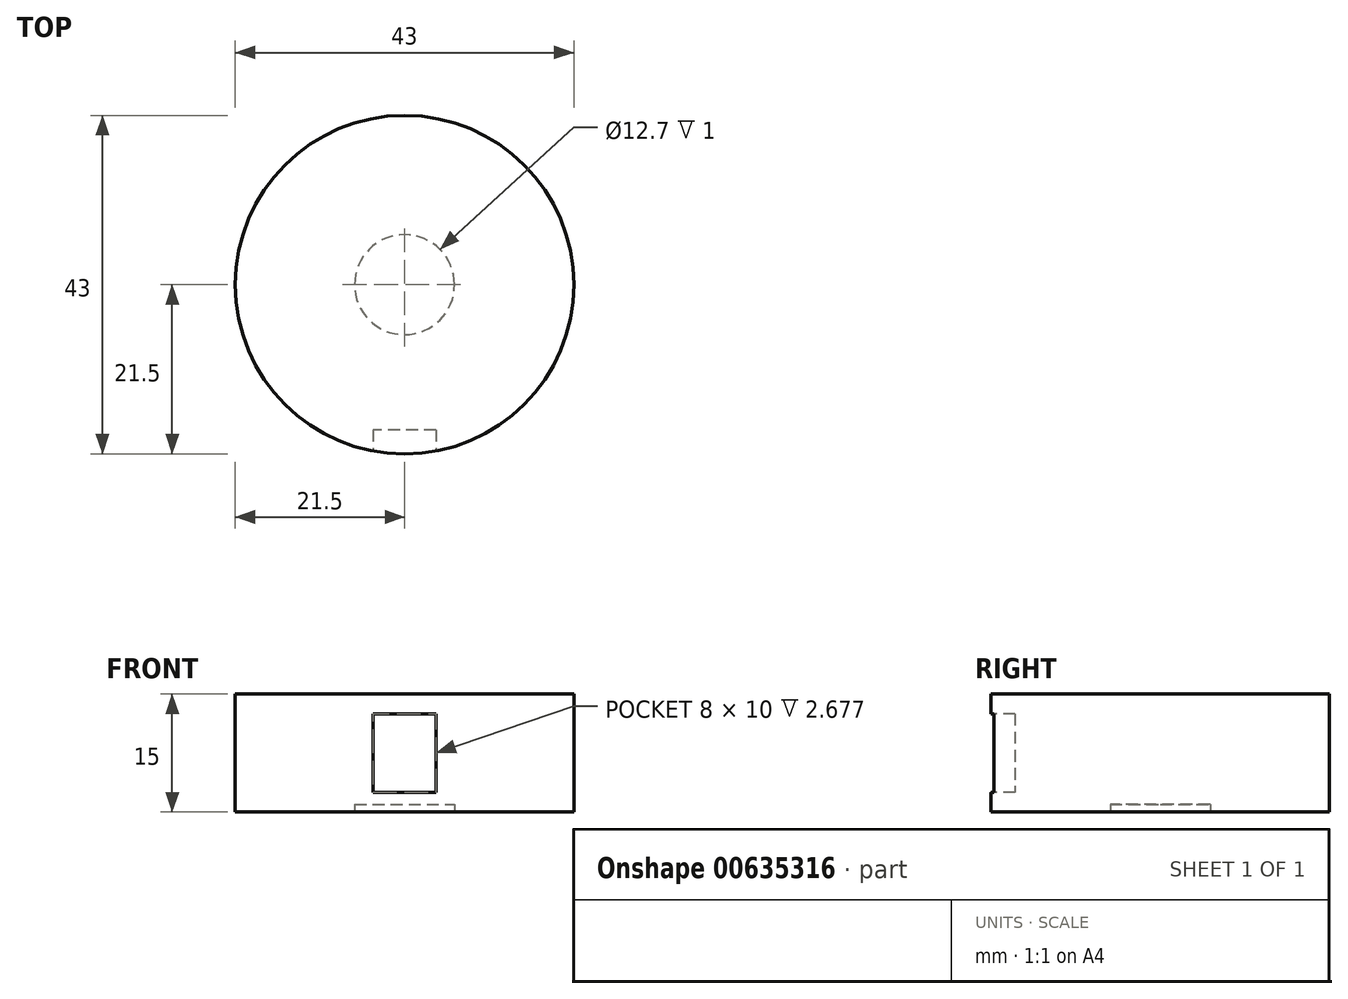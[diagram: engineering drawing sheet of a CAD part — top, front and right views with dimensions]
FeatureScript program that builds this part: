
annotation { "Feature Type Name" : "Feature", "Feature Type Description" : "" }
export const myFeature = defineFeature(function(context is Context, id is Id, definition is map)
    precondition{}
    {
        {
            var Q0;
            Q0=qCreatedBy(makeId("Top.planeOp"),FACE);
            var sketch = newSketch(context, id + "F0", { "sketchPlane" : qUnion([Q0])});
            skCircle(sketch, "E0", {"center": v(0, 0) * mm, "radius": 21.5 * mm});
            skSolve(sketch);
        }
        {
            var Q0;
            Q0=makeQuery(id+"F0.imprint","IMPRINT",FACE,{"disambiguationData":[TD([[makeQuery(id+"F0.imprint","IMPRINT",EDGE,{"derivedFrom":sQuery(id+"F0.wireOp",EDGE,"E0")}),1.0]])]});
            extrude(context, id + "F1", {"entities" : qUnion([Q0]), "depth" : 15 * mm, "offsetDistance" : 25.4 * mm});
        }
        {
            var Q0;
            Q0=qCreatedBy(makeId("Front.planeOp"),FACE);
            cPlane(context, id + "F2", {"entities" : qUnion([Q0]), "cplaneType" : CPlaneType.OFFSET, "offset" : 28.45 * mm, "width" : 152.4 * mm, "height" : 152.4 * mm});
        }
        {
            var Q0;
            Q0=qCreatedBy(id+"F2.planeOp",FACE);
            var sketch = newSketch(context, id + "F3", { "sketchPlane" : qUnion([Q0])});
            skLineSegment(sketch, "E1.0", {"start": v(-21.5, 15) * mm, "end": v(21.5, 15) * mm, "construction": true});
            skLineSegment(sketch, "E2.0", {"start": v(-21.5, 0) * mm, "end": v(21.5, 0) * mm, "construction": true});
            skLineSegment(sketch, "E3", {"start": v(0, 15) * mm, "end": v(0, 0) * mm, "construction": true});
            skLineSegment(sketch, "E4.bottom", {"start": v(4, 12.5) * mm, "end": v(-4, 12.5) * mm});
            skLineSegment(sketch, "E4.top", {"start": v(4, 2.5) * mm, "end": v(-4, 2.5) * mm});
            skLineSegment(sketch, "E4.left", {"start": v(4, 12.5) * mm, "end": v(4, 2.5) * mm});
            skLineSegment(sketch, "E4.right", {"start": v(-4, 12.5) * mm, "end": v(-4, 2.5) * mm});
            skPoint(sketch, "E4.middle", {"position": v(0, 7.5) * mm});
            skSolve(sketch);
        }
        {
            var Q0;
            Q0 = qSketchRegion(id + "F3", true);
            extrude(context, id + "F4", {"entities" : qUnion([Q0]), "operationType" : NewBodyOperationType.REMOVE, "oppositeDirection" : true, "depth" : 10 * mm, "offsetDistance" : 25.4 * mm});
        }
        {
            var Q0;
            Q0=makeQuery(id+"F1.opExtrude","CAP_FACE",FACE,{"disambiguationData":[OSD([sQuery(id+"F0.wireOp",EDGE,"E0")])],"isStart":true});
            var sketch = newSketch(context, id + "F5", { "sketchPlane" : qUnion([Q0])});
            skCircle(sketch, "E5", {"center": v(0, 0) * mm, "radius": 6.35 * mm});
            skSolve(sketch);
        }
        {
            var Q0;
            Q0 = qSketchRegion(id + "F5", true);
            extrude(context, id + "F6", {"entities" : qUnion([Q0]), "operationType" : NewBodyOperationType.REMOVE, "oppositeDirection" : true, "depth" : 1 * mm, "offsetDistance" : 25.4 * mm});
        }
    });
